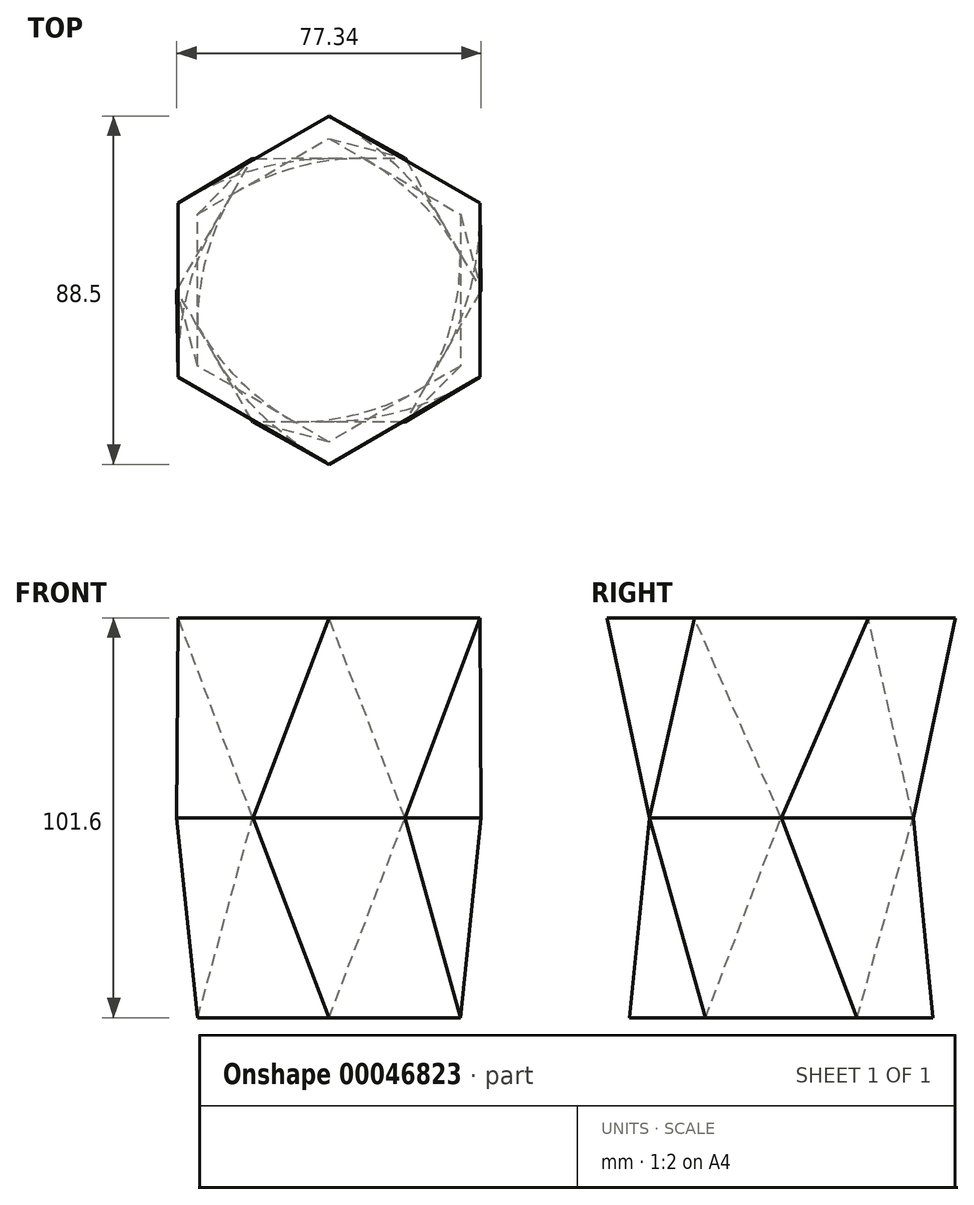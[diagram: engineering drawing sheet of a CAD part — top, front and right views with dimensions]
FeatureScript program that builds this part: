
annotation { "Feature Type Name" : "Feature", "Feature Type Description" : "" }
export const myFeature = defineFeature(function(context is Context, id is Id, definition is map)
    precondition{}
    {
        {
            var Q0;
            Q0=qCreatedBy(makeId("Top.planeOp"),FACE);
            var sketch = newSketch(context, id + "F0", { "sketchPlane" : qUnion([Q0])});
            skCircle(sketch, "E0.cCircle", {"center": v(0, 0) * mm, "radius": 33.37 * mm, "construction": true});
            skLineSegment(sketch, "E0.0", {"start": v(-33.37, -19.27) * mm, "end": v(-33.37, 19.27) * mm});
            skLineSegment(sketch, "E0.1", {"start": v(-33.37, 19.27) * mm, "end": v(0, 38.54) * mm});
            skLineSegment(sketch, "E0.2", {"start": v(0, 38.54) * mm, "end": v(33.37, 19.27) * mm});
            skLineSegment(sketch, "E0.3", {"start": v(33.37, 19.27) * mm, "end": v(33.37, -19.27) * mm});
            skLineSegment(sketch, "E0.4", {"start": v(33.37, -19.27) * mm, "end": v(0, -38.54) * mm});
            skLineSegment(sketch, "E0.5", {"start": v(0, -38.54) * mm, "end": v(-33.37, -19.27) * mm});
            skPoint(sketch, "E0.0.midPoint", {"position": v(-33.37, 0) * mm});
            skSolve(sketch);
        }
        {
            var Q0;
            Q0=qCreatedBy(makeId("Top.planeOp"),FACE);
            cPlane(context, id + "F1", {"entities" : qUnion([Q0]), "cplaneType" : CPlaneType.OFFSET, "offset" : 50.8 * mm, "width" : 152.4 * mm, "height" : 152.4 * mm});
        }
        {
            var Q0;
            Q0=qCreatedBy(id+"F1.planeOp",FACE);
            var sketch = newSketch(context, id + "F2", { "sketchPlane" : qUnion([Q0])});
            skCircle(sketch, "E1.cCircle", {"center": v(0, 0) * mm, "radius": 33.49 * mm, "construction": true});
            skLineSegment(sketch, "E1.0", {"start": v(-19.3, -33.5) * mm, "end": v(-38.67, -0.04) * mm});
            skLineSegment(sketch, "E1.1", {"start": v(-38.67, -0.04) * mm, "end": v(-19.37, 33.47) * mm});
            skLineSegment(sketch, "E1.2", {"start": v(-19.37, 33.47) * mm, "end": v(19.3, 33.5) * mm});
            skLineSegment(sketch, "E1.3", {"start": v(19.3, 33.5) * mm, "end": v(38.67, 0.04) * mm});
            skLineSegment(sketch, "E1.4", {"start": v(38.67, 0.04) * mm, "end": v(19.37, -33.47) * mm});
            skLineSegment(sketch, "E1.5", {"start": v(19.37, -33.47) * mm, "end": v(-19.3, -33.5) * mm});
            skPoint(sketch, "E1.0.midPoint", {"position": v(-28.98, -16.77) * mm});
            skSolve(sketch);
        }
        {
            var Q0;
            Q0=makeQuery(id+"F0.imprint","IMPRINT",FACE,{"disambiguationData":[TD([[makeQuery(id+"F0.imprint","IMPRINT",EDGE,{"derivedFrom":sQuery(id+"F0.wireOp",EDGE,"E0.0")}),-1.0]])]});
            var Q1;
            Q1=makeQuery(id+"F2.imprint","IMPRINT",FACE,{"disambiguationData":[TD([[makeQuery(id+"F2.imprint","IMPRINT",EDGE,{"derivedFrom":sQuery(id+"F2.wireOp",EDGE,"E1.0")}),-1.0]])]});
            loft(context, id + "F3", {"sheetProfilesArray" : [{ "sheetProfileEntities" : qUnion([Q0]) }, { "sheetProfileEntities" : qUnion([Q1]) }]});
        }
        {
            var Q0;
            Q0=makeQuery(id+"F3.opLoft","CAP_FACE",FACE,{"disambiguationData":[OSD([makeQuery(id+"F2.imprint","IMPRINT",FACE,{"disambiguationData":[TD([[makeQuery(id+"F2.imprint","IMPRINT",EDGE,{"derivedFrom":sQuery(id+"F2.wireOp",EDGE,"E1.0")}),-1.0]])]})])],"isStart":true});
            cPlane(context, id + "F4", {"entities" : qUnion([Q0]), "cplaneType" : CPlaneType.OFFSET, "offset" : 50.8 * mm, "width" : 152.4 * mm, "height" : 152.4 * mm});
        }
        {
            var Q0;
            Q0=qCreatedBy(id+"F4.planeOp",FACE);
            var sketch = newSketch(context, id + "F5", { "sketchPlane" : qUnion([Q0])});
            skCircle(sketch, "E2.cCircle", {"center": v(0, 0) * mm, "radius": 38.32 * mm, "construction": true});
            skLineSegment(sketch, "E2.0", {"start": v(-38.32, -22.12) * mm, "end": v(-38.32, 22.12) * mm});
            skLineSegment(sketch, "E2.1", {"start": v(-38.32, 22.12) * mm, "end": v(0, 44.25) * mm});
            skLineSegment(sketch, "E2.2", {"start": v(0, 44.25) * mm, "end": v(38.32, 22.12) * mm});
            skLineSegment(sketch, "E2.3", {"start": v(38.32, 22.12) * mm, "end": v(38.32, -22.12) * mm});
            skLineSegment(sketch, "E2.4", {"start": v(38.32, -22.12) * mm, "end": v(0, -44.25) * mm});
            skLineSegment(sketch, "E2.5", {"start": v(0, -44.25) * mm, "end": v(-38.32, -22.12) * mm});
            skPoint(sketch, "E2.0.midPoint", {"position": v(-38.32, 0) * mm});
            skSolve(sketch);
        }
        {
            var Q1;
            Q1=makeQuery(id+"F3.opLoft","CAP_FACE",FACE,{"disambiguationData":[OSD([makeQuery(id+"F2.imprint","IMPRINT",FACE,{"disambiguationData":[TD([[makeQuery(id+"F2.imprint","IMPRINT",EDGE,{"derivedFrom":sQuery(id+"F2.wireOp",EDGE,"E1.0")}),-1.0]])]})])],"isStart":true});
            var Q2;
            Q2=makeQuery(id+"F5.imprint","IMPRINT",FACE,{"disambiguationData":[TD([[makeQuery(id+"F5.imprint","IMPRINT",EDGE,{"derivedFrom":sQuery(id+"F5.wireOp",EDGE,"E2.0")}),-1.0]])]});
            loft(context, id + "F6", {"operationType" : NewBodyOperationType.ADD, "sheetProfilesArray" : [{ "sheetProfileEntities" : qUnion([Q1]) }, { "sheetProfileEntities" : qUnion([Q2]) }]});
        }
    });
